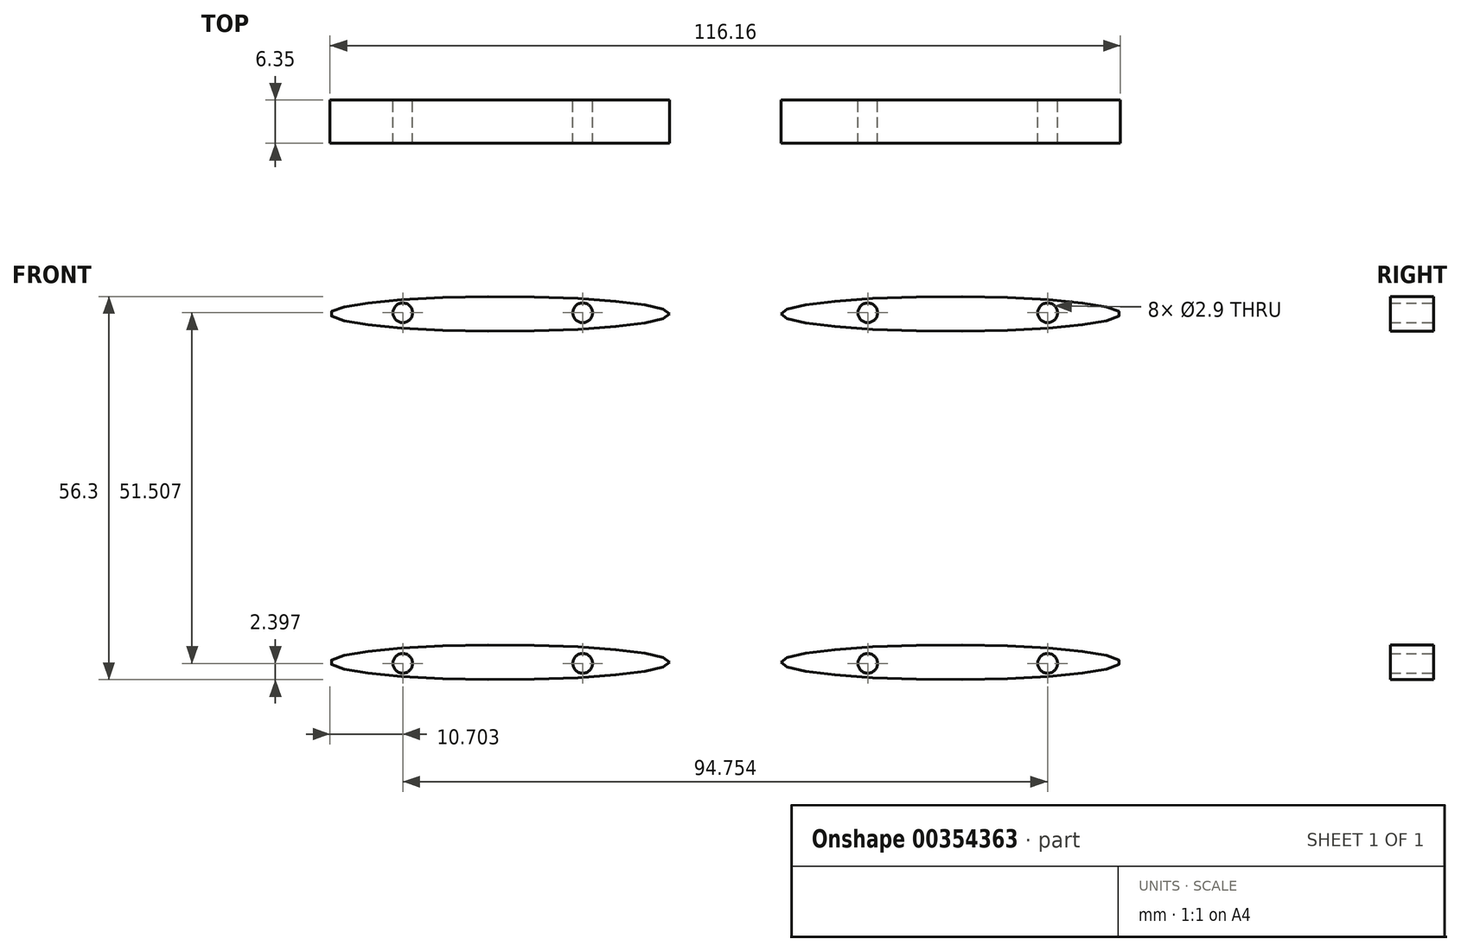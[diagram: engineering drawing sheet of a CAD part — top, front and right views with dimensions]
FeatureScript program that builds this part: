
annotation { "Feature Type Name" : "Feature", "Feature Type Description" : "" }
export const myFeature = defineFeature(function(context is Context, id is Id, definition is map)
    precondition{}
    {
        {
            var Q0;
            Q0=qCreatedBy(makeId("Front.planeOp"),FACE);
            var sketch = newSketch(context, id + "F0", { "sketchPlane" : qUnion([Q0])});
            skEllipse(sketch, "E0", {"center": v(-33.14, 25.6) * mm, "majorRadius": 24.94 * mm, "minorRadius": 2.55 * mm, "majorAxis": v(1, 0)});
            skCircle(sketch, "E1", {"center": v(-47.38, 25.75) * mm, "radius": 1.45 * mm});
            skCircle(sketch, "E2", {"center": v(-20.94, 25.75) * mm, "radius": 1.45 * mm});
            skLineSegment(sketch, "E3", {"start": v(0, 76.73) * mm, "end": v(0, -75.12) * mm});
            skLineSegment(sketch, "E4", {"start": v(-76.14, 0) * mm, "end": v(76.1, 0) * mm});
            skCircle(sketch, "E5.MirrorC", {"center": v(20.94, 25.75) * mm, "radius": 1.45 * mm});
            skCircle(sketch, "E6.MirrorC", {"center": v(47.38, 25.75) * mm, "radius": 1.45 * mm});
            skEllipse(sketch, "E7.MirrorC", {"center": v(33.14, 25.6) * mm, "majorRadius": 24.94 * mm, "minorRadius": 2.55 * mm, "majorAxis": v(-1, 0)});
            skCircle(sketch, "E8.MirrorC", {"center": v(-20.94, -25.75) * mm, "radius": 1.45 * mm});
            skCircle(sketch, "E9.MirrorC", {"center": v(-47.38, -25.75) * mm, "radius": 1.45 * mm});
            skEllipse(sketch, "E10.MirrorC", {"center": v(-33.14, -25.6) * mm, "majorRadius": 24.94 * mm, "minorRadius": 2.55 * mm, "majorAxis": v(1, 0)});
            skCircle(sketch, "E11.MirrorC", {"center": v(20.94, -25.75) * mm, "radius": 1.45 * mm});
            skEllipse(sketch, "E12.MirrorC", {"center": v(33.14, -25.6) * mm, "majorRadius": 24.94 * mm, "minorRadius": 2.55 * mm, "majorAxis": v(-1, 0)});
            skCircle(sketch, "E13.MirrorC", {"center": v(47.38, -25.75) * mm, "radius": 1.45 * mm});
            skSolve(sketch);
        }
        {
            var Q0;
            Q0 = qSketchRegion(id + "F0", true);
            extrude(context, id + "F1", {"entities" : qUnion([Q0]), "depth" : 6.35 * mm});
        }
    });
